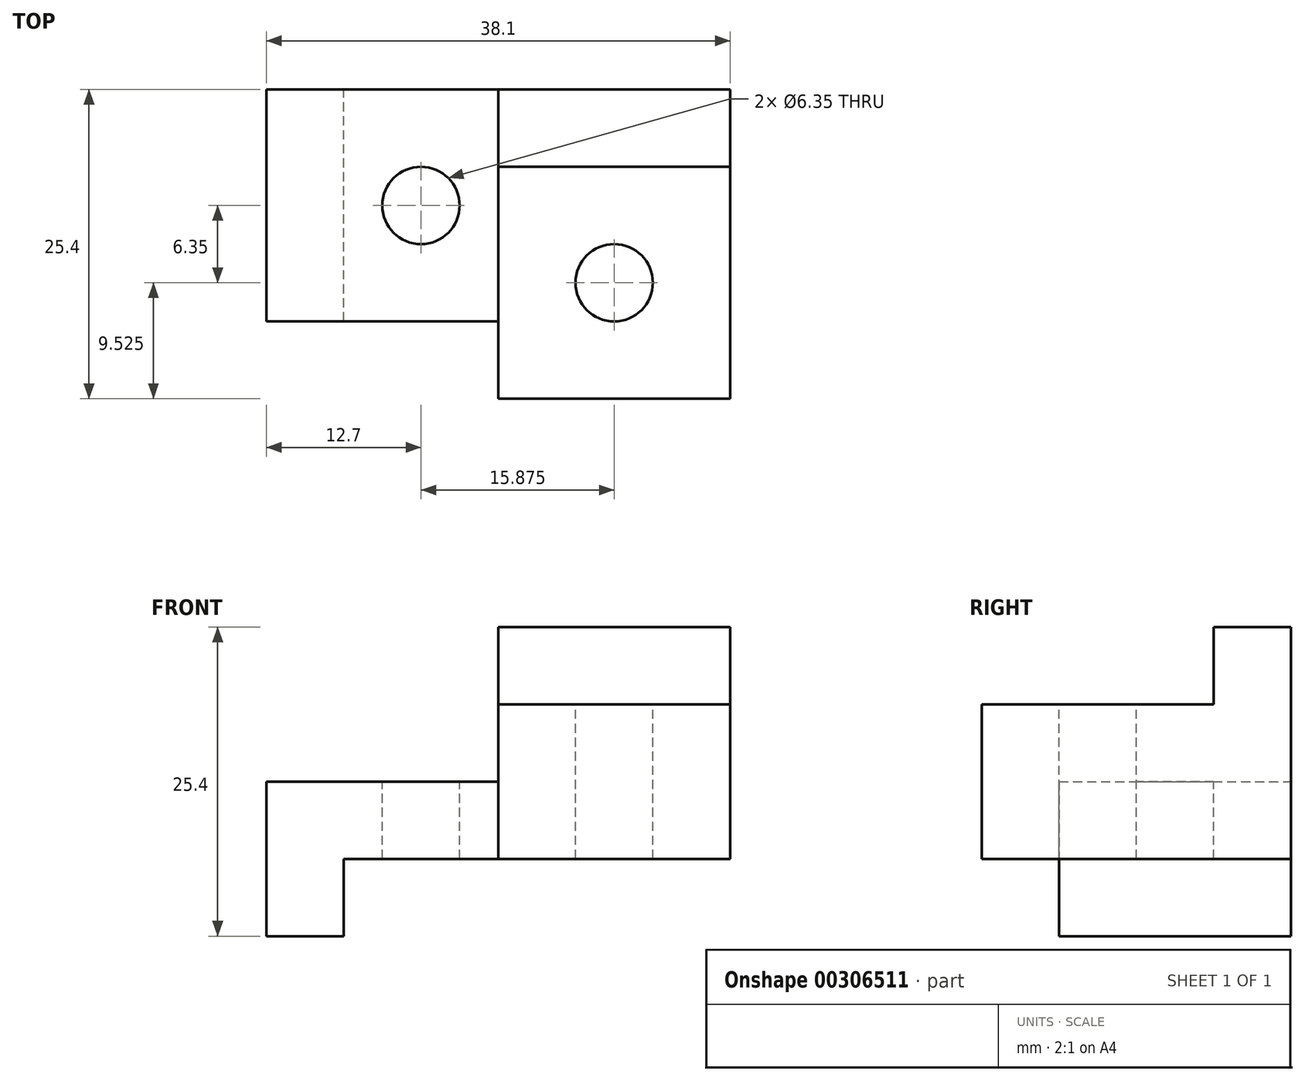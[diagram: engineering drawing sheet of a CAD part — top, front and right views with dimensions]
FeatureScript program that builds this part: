
annotation { "Feature Type Name" : "Feature", "Feature Type Description" : "" }
export const myFeature = defineFeature(function(context is Context, id is Id, definition is map)
    precondition{}
    {
        {
            var Q0;
            Q0=qCreatedBy(makeId("Front.planeOp"),FACE);
            var sketch = newSketch(context, id + "F0", { "sketchPlane" : qUnion([Q0])});
            skLineSegment(sketch, "E0", {"start": v(0, 0) * mm, "end": v(0, 6.35) * mm});
            skLineSegment(sketch, "E1", {"start": v(0, 6.35) * mm, "end": v(19.05, 6.35) * mm});
            skLineSegment(sketch, "E2", {"start": v(19.05, 6.35) * mm, "end": v(19.05, 0) * mm});
            skLineSegment(sketch, "E3", {"start": v(19.05, 0) * mm, "end": v(6.35, 0) * mm});
            skLineSegment(sketch, "E4", {"start": v(6.35, 0) * mm, "end": v(6.35, -6.35) * mm});
            skLineSegment(sketch, "E5", {"start": v(6.35, -6.35) * mm, "end": v(0, -6.35) * mm});
            skLineSegment(sketch, "E6", {"start": v(0, -6.35) * mm, "end": v(0, 0) * mm});
            skLineSegment(sketch, "E7", {"start": v(19.05, 0) * mm, "end": v(19.05, 12.7) * mm});
            skPoint(sketch, "E7.endSnap0", {"position": v(19.05, 3.18) * mm});
            skLineSegment(sketch, "E8", {"start": v(19.05, 12.7) * mm, "end": v(38.1, 12.7) * mm});
            skLineSegment(sketch, "E9", {"start": v(38.1, 12.7) * mm, "end": v(38.1, 0) * mm});
            skLineSegment(sketch, "E10", {"start": v(38.1, 0) * mm, "end": v(19.05, 0) * mm});
            skLineSegment(sketch, "E11", {"start": v(19.05, 12.7) * mm, "end": v(19.05, 19.05) * mm});
            skLineSegment(sketch, "E12", {"start": v(19.05, 19.05) * mm, "end": v(38.1, 19.05) * mm});
            skLineSegment(sketch, "E13", {"start": v(38.1, 19.05) * mm, "end": v(38.1, 12.7) * mm});
            skSolve(sketch);
        }
        {
            var Q0;
            Q0=makeQuery(id+"F0.imprint","IMPRINT",FACE,{"disambiguationData":[TD([[makeQuery(id+"F0.imprint","IMPRINT",EDGE,{"derivedFrom":sQuery(id+"F0.wireOp",EDGE,"E0")}),-1.0]])]});
            extrude(context, id + "F1", {"entities" : qUnion([Q0]), "depth" : 19.05 * mm});
        }
        {
            var Q0;
            {var subQ0=sQuery(id+"F0.wireOp",EDGE,"E8");Q0=makeQuery(id+"F0.imprint","IMPRINT",FACE,{"disambiguationData":[TD([[makeQuery(id+"F0.imprint","IMPRINT",EDGE,{"derivedFrom":subQ0}),-1.0]])]});}
            extrude(context, id + "F2", {"entities" : qUnion([Q0]), "operationType" : NewBodyOperationType.ADD, "depth" : 25.4 * mm});
        }
        {
            var Q0;
            Q0=makeQuery(id+"F0.imprint","IMPRINT",FACE,{"disambiguationData":[TD([[makeQuery(id+"F0.imprint","IMPRINT",EDGE,{"derivedFrom":sQuery(id+"F0.wireOp",EDGE,"E8")}),1.0]])]});
            extrude(context, id + "F3", {"entities" : qUnion([Q0]), "operationType" : NewBodyOperationType.ADD, "depth" : 6.35 * mm});
        }
        {
            var Q0;
            Q0=makeQuery(id+"F2.opExtrude","SWEPT_FACE",FACE,{"disambiguationData":[OSD([sQuery(id+"F0.wireOp",EDGE,"E8")])]});
            var sketch = newSketch(context, id + "F4", { "sketchPlane" : qUnion([Q0])});
            skCircle(sketch, "E14", {"center": v(12.7, -9.53) * mm, "radius": 3.18 * mm});
            skCircle(sketch, "E15", {"center": v(28.58, -15.88) * mm, "radius": 3.18 * mm});
            skSolve(sketch);
        }
        {
            var Q0;
            Q0 = qSketchRegion(id + "F4", true);
            extrude(context, id + "F5", {"entities" : qUnion([Q0]), "operationType" : NewBodyOperationType.REMOVE, "endBound" : BoundingType.THROUGH_ALL, "oppositeDirection" : true, "depth" : 25.4 * mm});
        }
    });
